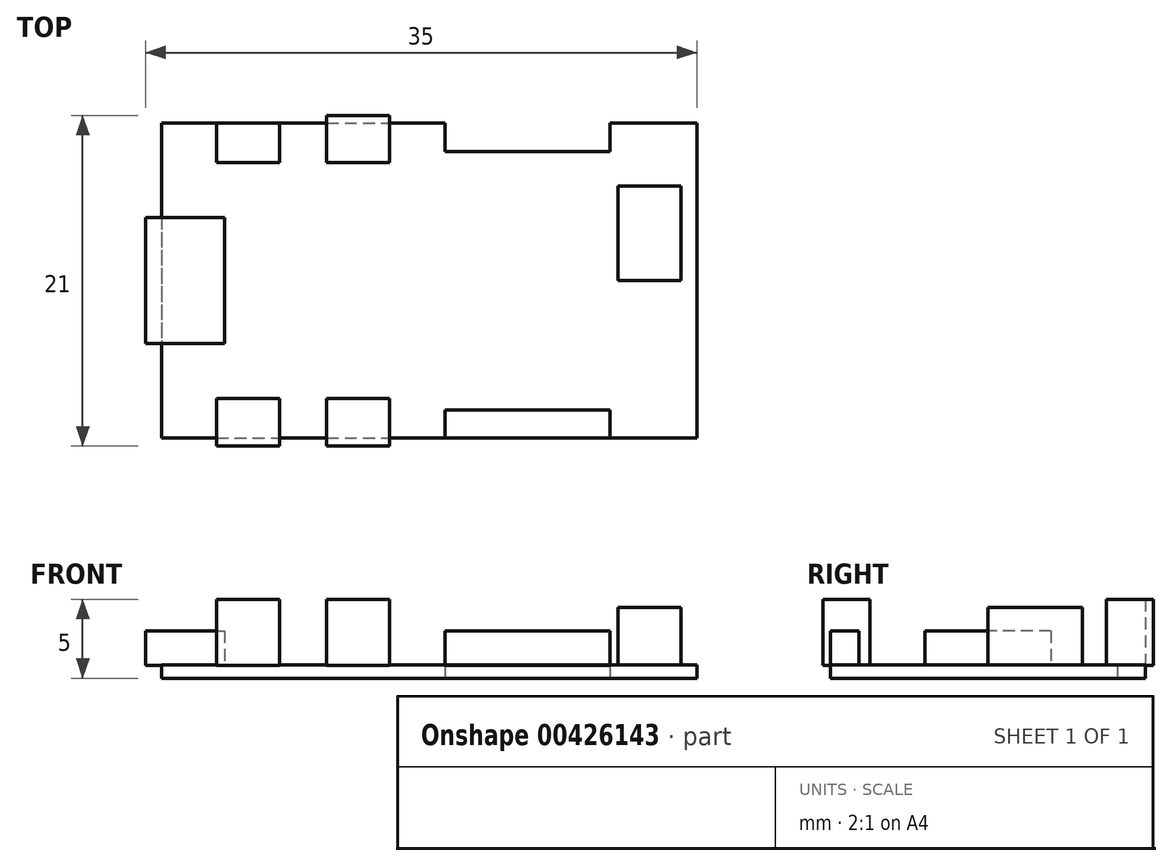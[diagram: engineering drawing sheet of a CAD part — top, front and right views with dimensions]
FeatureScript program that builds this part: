
annotation { "Feature Type Name" : "Feature", "Feature Type Description" : "" }
export const myFeature = defineFeature(function(context is Context, id is Id, definition is map)
    precondition{}
    {
        {
            var Q0;
            Q0=qCreatedBy(makeId("Top.planeOp"),FACE);
            var sketch = newSketch(context, id + "F0", { "sketchPlane" : qUnion([Q0])});
            skLineSegment(sketch, "E0.bottom", {"start": v(-17, 10) * mm, "end": v(17, 10) * mm});
            skLineSegment(sketch, "E0.top", {"start": v(-17, -10) * mm, "end": v(17, -10) * mm});
            skLineSegment(sketch, "E0.left", {"start": v(-17, 10) * mm, "end": v(-17, -10) * mm});
            skLineSegment(sketch, "E0.right", {"start": v(17, 10) * mm, "end": v(17, -10) * mm});
            skPoint(sketch, "E0.middle", {"position": v(0, 0) * mm});
            skLineSegment(sketch, "E1.bottom", {"start": v(11.5, 10) * mm, "end": v(1, 10) * mm});
            skLineSegment(sketch, "E1.top", {"start": v(11.5, 8.2) * mm, "end": v(1, 8.2) * mm});
            skLineSegment(sketch, "E1.left", {"start": v(11.5, 10) * mm, "end": v(11.5, 8.2) * mm});
            skLineSegment(sketch, "E1.right", {"start": v(1, 10) * mm, "end": v(1, 8.2) * mm});
            skLineSegment(sketch, "E2.MirrorCS", {"start": v(11.5, -8.2) * mm, "end": v(1, -8.2) * mm});
            skLineSegment(sketch, "E3.MirrorCS", {"start": v(1, -10) * mm, "end": v(1, -8.2) * mm});
            skLineSegment(sketch, "E4.MirrorCS", {"start": v(11.5, -10) * mm, "end": v(11.5, -8.2) * mm});
            skLineSegment(sketch, "E5.MirrorCS", {"start": v(11.5, -10) * mm, "end": v(1, -10) * mm});
            skLineSegment(sketch, "E6.bottom", {"start": v(12, 6) * mm, "end": v(16, 6) * mm});
            skLineSegment(sketch, "E6.top", {"start": v(12, 0) * mm, "end": v(16, 0) * mm});
            skLineSegment(sketch, "E6.left", {"start": v(12, 6) * mm, "end": v(12, 0) * mm});
            skLineSegment(sketch, "E6.right", {"start": v(16, 6) * mm, "end": v(16, 0) * mm});
            skPoint(sketch, "E6.middle", {"position": v(14, 3) * mm});
            skLineSegment(sketch, "E7.bottom", {"start": v(-18, 4) * mm, "end": v(-13, 4) * mm});
            skLineSegment(sketch, "E7.top", {"start": v(-18, -4) * mm, "end": v(-13, -4) * mm});
            skLineSegment(sketch, "E7.left", {"start": v(-18, 4) * mm, "end": v(-18, -4) * mm});
            skLineSegment(sketch, "E7.right", {"start": v(-13, 4) * mm, "end": v(-13, -4) * mm});
            skPoint(sketch, "E7.middle", {"position": v(-15.5, 0) * mm});
            skLineSegment(sketch, "E8.bottom", {"start": v(-13.5, 10.5) * mm, "end": v(-9.5, 10.5) * mm});
            skLineSegment(sketch, "E8.top", {"start": v(-13.5, 7.5) * mm, "end": v(-9.5, 7.5) * mm});
            skLineSegment(sketch, "E8.left", {"start": v(-13.5, 10.5) * mm, "end": v(-13.5, 7.5) * mm});
            skLineSegment(sketch, "E8.right", {"start": v(-9.5, 10.5) * mm, "end": v(-9.5, 7.5) * mm});
            skPoint(sketch, "E8.middle", {"position": v(-11.5, 9) * mm});
            skLineSegment(sketch, "E9.bottom", {"start": v(-6.5, 10.5) * mm, "end": v(-2.5, 10.5) * mm});
            skLineSegment(sketch, "E9.top", {"start": v(-6.5, 7.5) * mm, "end": v(-2.5, 7.5) * mm});
            skLineSegment(sketch, "E9.left", {"start": v(-6.5, 10.5) * mm, "end": v(-6.5, 7.5) * mm});
            skLineSegment(sketch, "E9.right", {"start": v(-2.5, 10.5) * mm, "end": v(-2.5, 7.5) * mm});
            skPoint(sketch, "E9.middle", {"position": v(-4.5, 9) * mm});
            skLineSegment(sketch, "E10.MirrorCS", {"start": v(-6.5, -7.5) * mm, "end": v(-2.5, -7.5) * mm});
            skLineSegment(sketch, "E11.MirrorCS", {"start": v(-2.5, -10.5) * mm, "end": v(-2.5, -7.5) * mm});
            skLineSegment(sketch, "E12.MirrorCS", {"start": v(-6.5, -10.5) * mm, "end": v(-6.5, -7.5) * mm});
            skLineSegment(sketch, "E13.MirrorCS", {"start": v(-13.5, -7.5) * mm, "end": v(-9.5, -7.5) * mm});
            skLineSegment(sketch, "E14.MirrorCS", {"start": v(-9.5, -10.5) * mm, "end": v(-9.5, -7.5) * mm});
            skLineSegment(sketch, "E15.MirrorCS", {"start": v(-13.5, -10.5) * mm, "end": v(-13.5, -7.5) * mm});
            skLineSegment(sketch, "E16.MirrorCS", {"start": v(-13.5, -10.5) * mm, "end": v(-9.5, -10.5) * mm});
            skLineSegment(sketch, "E17.MirrorCS", {"start": v(-6.5, -10.5) * mm, "end": v(-2.5, -10.5) * mm});
            skSolve(sketch);
        }
        {
            var Q0;
            Q0=makeQuery(id+"F0.imprint","IMPRINT",FACE,{"disambiguationData":[TD([[makeQuery(id+"F0.imprint","IMPRINT",EDGE,{"derivedFrom":sQuery(id+"F0.wireOp",EDGE,"E0.bottom")}),-1.0]])]});
            var Q1;
            Q1=makeQuery(id+"F0.imprint","IMPRINT",FACE,{"disambiguationData":[TD([[makeQuery(id+"F0.imprint","IMPRINT",EDGE,{"derivedFrom":sQuery(id+"F0.wireOp",EDGE,"E2.MirrorCS")}),1.0]])]});
            var Q2;
            Q2=makeQuery(id+"F0.imprint","IMPRINT",FACE,{"disambiguationData":[TD([[makeQuery(id+"F0.imprint","IMPRINT",EDGE,{"derivedFrom":sQuery(id+"F0.wireOp",EDGE,"E1.bottom")}),1.0]])]});
            var Q3;
            {var subQ5=sQuery(id+"F0.wireOp",EDGE,"E7.right");Q3=makeQuery(id+"F0.imprint","IMPRINT",FACE,{"disambiguationData":[TD([[makeQuery(id+"F0.imprint","IMPRINT",EDGE,{"derivedFrom":subQ5}),-1.0]])]});}
            var Q4;
            Q4=makeQuery(id+"F0.imprint","IMPRINT",FACE,{"disambiguationData":[TD([[makeQuery(id+"F0.imprint","IMPRINT",EDGE,{"derivedFrom":sQuery(id+"F0.wireOp",EDGE,"E6.bottom")}),-1.0]])]});
            var Q5;
            {var subQ5=sQuery(id+"F0.wireOp",EDGE,"E10.MirrorCS");Q5=makeQuery(id+"F0.imprint","IMPRINT",FACE,{"disambiguationData":[TD([[makeQuery(id+"F0.imprint","IMPRINT",EDGE,{"derivedFrom":subQ5}),-1.0]])]});}
            var Q6;
            {var subQ5=sQuery(id+"F0.wireOp",EDGE,"E13.MirrorCS");Q6=makeQuery(id+"F0.imprint","IMPRINT",FACE,{"disambiguationData":[TD([[makeQuery(id+"F0.imprint","IMPRINT",EDGE,{"derivedFrom":subQ5}),-1.0]])]});}
            var Q7;
            {var subQ5=sQuery(id+"F0.wireOp",EDGE,"E8.top");Q7=makeQuery(id+"F0.imprint","IMPRINT",FACE,{"disambiguationData":[TD([[makeQuery(id+"F0.imprint","IMPRINT",EDGE,{"derivedFrom":subQ5}),1.0]])]});}
            var Q8;
            {var subQ5=sQuery(id+"F0.wireOp",EDGE,"E9.top");Q8=makeQuery(id+"F0.imprint","IMPRINT",FACE,{"disambiguationData":[TD([[makeQuery(id+"F0.imprint","IMPRINT",EDGE,{"derivedFrom":subQ5}),1.0]])]});}
            extrude(context, id + "F1", {"entities" : qUnion([Q0, Q1, Q2, Q3, Q4, Q5, Q6, Q7, Q8]), "depth" : .85 * mm});
        }
        {
            var Q0;
            Q0=makeQuery(id+"F0.imprint","IMPRINT",FACE,{"disambiguationData":[TD([[makeQuery(id+"F0.imprint","IMPRINT",EDGE,{"derivedFrom":sQuery(id+"F0.wireOp",EDGE,"E2.MirrorCS")}),1.0]])]});
            var Q1;
            Q1=makeQuery(id+"F0.imprint","IMPRINT",FACE,{"disambiguationData":[TD([[makeQuery(id+"F0.imprint","IMPRINT",EDGE,{"derivedFrom":sQuery(id+"F0.wireOp",EDGE,"E1.bottom")}),1.0]])]});
            extrude(context, id + "F2", {"entities" : qUnion([Q0, Q1]), "depth" : 3 * mm, "hasSecondDirection" : true, "secondDirectionOppositeDirection" : false, "secondDirectionDepth" : .8 * mm});
        }
        {
            var Q0;
            Q0=makeQuery(id+"F0.imprint","IMPRINT",FACE,{"disambiguationData":[TD([[makeQuery(id+"F0.imprint","IMPRINT",EDGE,{"derivedFrom":sQuery(id+"F0.wireOp",EDGE,"E6.bottom")}),-1.0]])]});
            extrude(context, id + "F3", {"entities" : qUnion([Q0]), "depth" : 4.5 * mm, "hasSecondDirection" : true, "secondDirectionOppositeDirection" : false, "secondDirectionDepth" : .8 * mm});
        }
        {
            var Q0;
            {var subQ5=sQuery(id+"F0.wireOp",EDGE,"E7.right");Q0=makeQuery(id+"F0.imprint","IMPRINT",FACE,{"disambiguationData":[TD([[makeQuery(id+"F0.imprint","IMPRINT",EDGE,{"derivedFrom":subQ5}),-1.0]])]});}
            var Q1;
            {var subQ5=sQuery(id+"F0.wireOp",EDGE,"E7.left");Q1=makeQuery(id+"F0.imprint","IMPRINT",FACE,{"disambiguationData":[TD([[makeQuery(id+"F0.imprint","IMPRINT",EDGE,{"derivedFrom":subQ5}),1.0]])]});}
            extrude(context, id + "F4", {"entities" : qUnion([Q0, Q1]), "depth" : 3 * mm, "hasSecondDirection" : true, "secondDirectionOppositeDirection" : false, "secondDirectionDepth" : .8 * mm});
        }
        {
            var Q0;
            {var subQ5=sQuery(id+"F0.wireOp",EDGE,"E13.MirrorCS");Q0=makeQuery(id+"F0.imprint","IMPRINT",FACE,{"disambiguationData":[TD([[makeQuery(id+"F0.imprint","IMPRINT",EDGE,{"derivedFrom":subQ5}),-1.0]])]});}
            var Q1;
            {var subQ5=sQuery(id+"F0.wireOp",EDGE,"E16.MirrorCS");Q1=makeQuery(id+"F0.imprint","IMPRINT",FACE,{"disambiguationData":[TD([[makeQuery(id+"F0.imprint","IMPRINT",EDGE,{"derivedFrom":subQ5}),1.0]])]});}
            var Q2;
            {var subQ5=sQuery(id+"F0.wireOp",EDGE,"E10.MirrorCS");Q2=makeQuery(id+"F0.imprint","IMPRINT",FACE,{"disambiguationData":[TD([[makeQuery(id+"F0.imprint","IMPRINT",EDGE,{"derivedFrom":subQ5}),-1.0]])]});}
            var Q3;
            {var subQ5=sQuery(id+"F0.wireOp",EDGE,"E17.MirrorCS");Q3=makeQuery(id+"F0.imprint","IMPRINT",FACE,{"disambiguationData":[TD([[makeQuery(id+"F0.imprint","IMPRINT",EDGE,{"derivedFrom":subQ5}),1.0]])]});}
            var Q4;
            {var subQ5=sQuery(id+"F0.wireOp",EDGE,"E9.top");Q4=makeQuery(id+"F0.imprint","IMPRINT",FACE,{"disambiguationData":[TD([[makeQuery(id+"F0.imprint","IMPRINT",EDGE,{"derivedFrom":subQ5}),1.0]])]});}
            var Q5;
            {var subQ5=sQuery(id+"F0.wireOp",EDGE,"E9.bottom");Q5=makeQuery(id+"F0.imprint","IMPRINT",FACE,{"disambiguationData":[TD([[makeQuery(id+"F0.imprint","IMPRINT",EDGE,{"derivedFrom":subQ5}),-1.0]])]});}
            var Q6;
            {var subQ5=sQuery(id+"F0.wireOp",EDGE,"E8.top");Q6=makeQuery(id+"F0.imprint","IMPRINT",FACE,{"disambiguationData":[TD([[makeQuery(id+"F0.imprint","IMPRINT",EDGE,{"derivedFrom":subQ5}),1.0]])]});}
            extrude(context, id + "F5", {"entities" : qUnion([Q0, Q1, Q2, Q3, Q4, Q5, Q6]), "depth" : 5 * mm, "hasSecondDirection" : true, "secondDirectionOppositeDirection" : false, "secondDirectionDepth" : .8 * mm});
        }
    });
